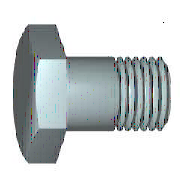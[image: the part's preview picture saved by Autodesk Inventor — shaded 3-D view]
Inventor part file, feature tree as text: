
AUTODESK INVENTOR PART (.ipt)
format: ipt  version: 2021 (Build 250183000, 183)  size: 192,512 bytes
history: native  units: mm (DEFAULTED — no unit token found)
features: sketch x3, extrude x1, chamfer x1, plane x1
ambient origin geometry x7: Origin, YZ Plane, XZ Plane, X Axis, Y Axis, Z Axis, Center Point
bodies: Solid1 (feature_tree), Body (feature_tree)
feature tree (6):
  extrude  "Head"  Depth=30.0mm
  chamfer  "Chamfer1"  Distance=6.9mm
  plane  "Work Plane1"
  sketch  "Sketch1"  dims[d0=50.0mm d1=30.0mm]
  sketch  "Sketch2"  dims[d2=12.0mm]
  sketch  "Sketch4"  dims[d12=90.0deg d3=6.9mm d4=0.0mm d5=30.0deg d21=90.0deg d6=1.073538mm d7=1.073638mm d8=0.0mm d9=0.6001mm d10=16.63mm d11=18.0mm d13=1.073638mm d14=12.0mm d15=30.0mm d16=0.0mm d19=18.0mm d55=45.0deg d57=0.0mm d58=0.0mm]
